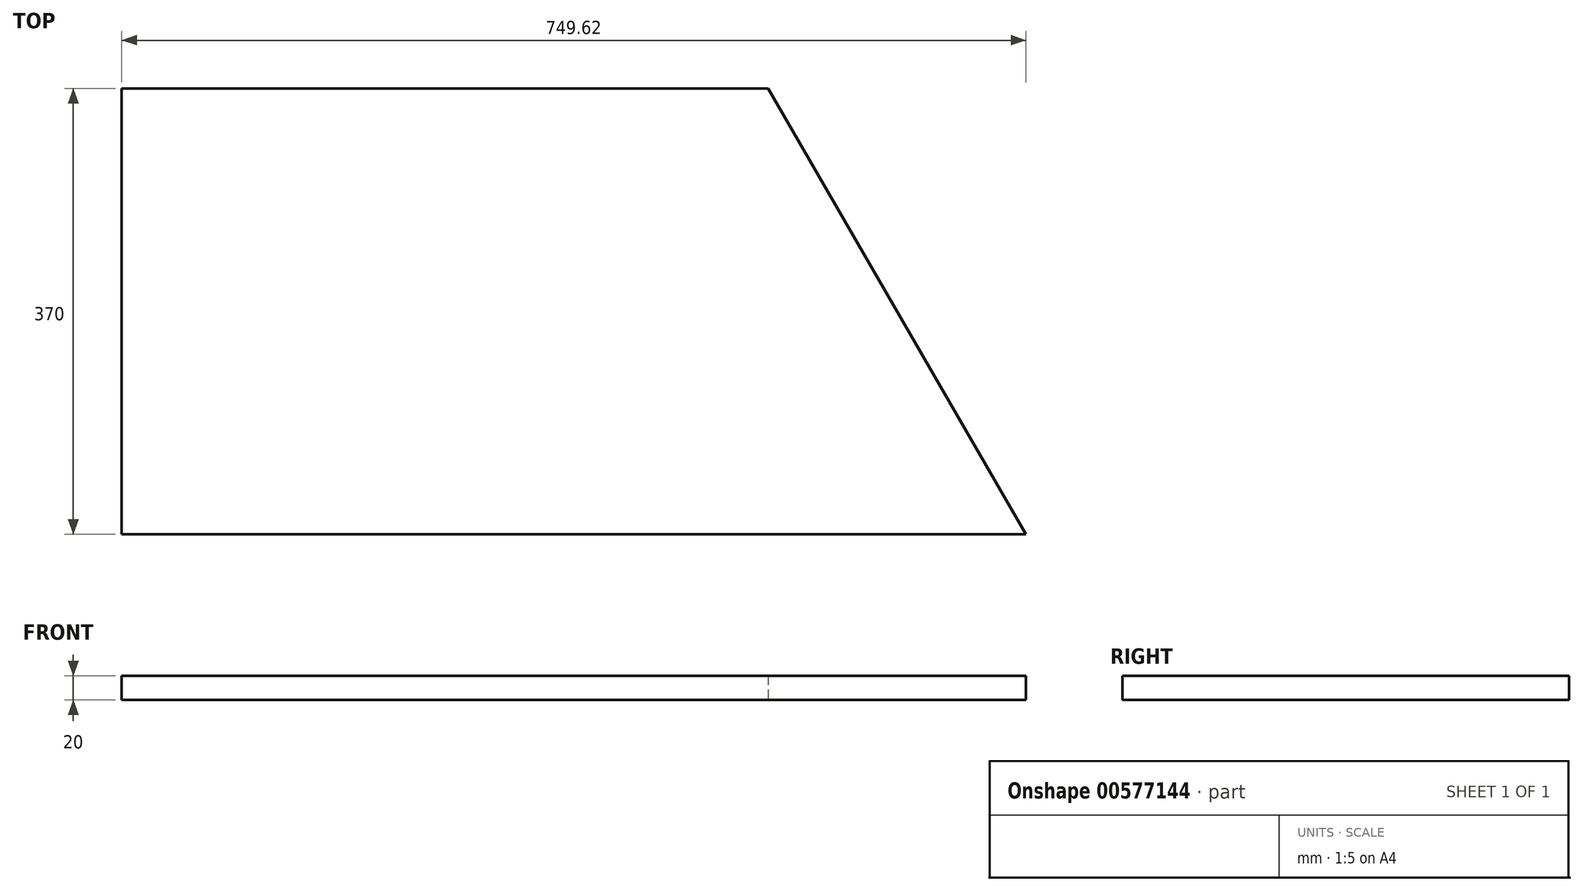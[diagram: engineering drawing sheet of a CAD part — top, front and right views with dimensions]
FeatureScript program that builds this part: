
annotation { "Feature Type Name" : "Feature", "Feature Type Description" : "" }
export const myFeature = defineFeature(function(context is Context, id is Id, definition is map)
    precondition{}
    {
        {
            var Q0;
            Q0=qCreatedBy(makeId("Top.planeOp"),FACE);
            var sketch = newSketch(context, id + "F0", { "sketchPlane" : qUnion([Q0])});
            skLineSegment(sketch, "E0", {"start": v(-495.16, 185.15) * mm, "end": v(-495.16, -184.85) * mm});
            skLineSegment(sketch, "E1", {"start": v(-495.16, -184.85) * mm, "end": v(254.46, -184.85) * mm});
            skLineSegment(sketch, "E2", {"start": v(254.46, -184.85) * mm, "end": v(40.84, 185.15) * mm});
            skLineSegment(sketch, "E3", {"start": v(40.84, 185.15) * mm, "end": v(-495.16, 185.15) * mm});
            skSolve(sketch);
        }
        {
            var Q0;
            Q0 = qSketchRegion(id + "F0", true);
            extrude(context, id + "F1", {"entities" : qUnion([Q0]), "depth" : 20 * mm, "offsetDistance" : 25 * mm});
        }
    });
